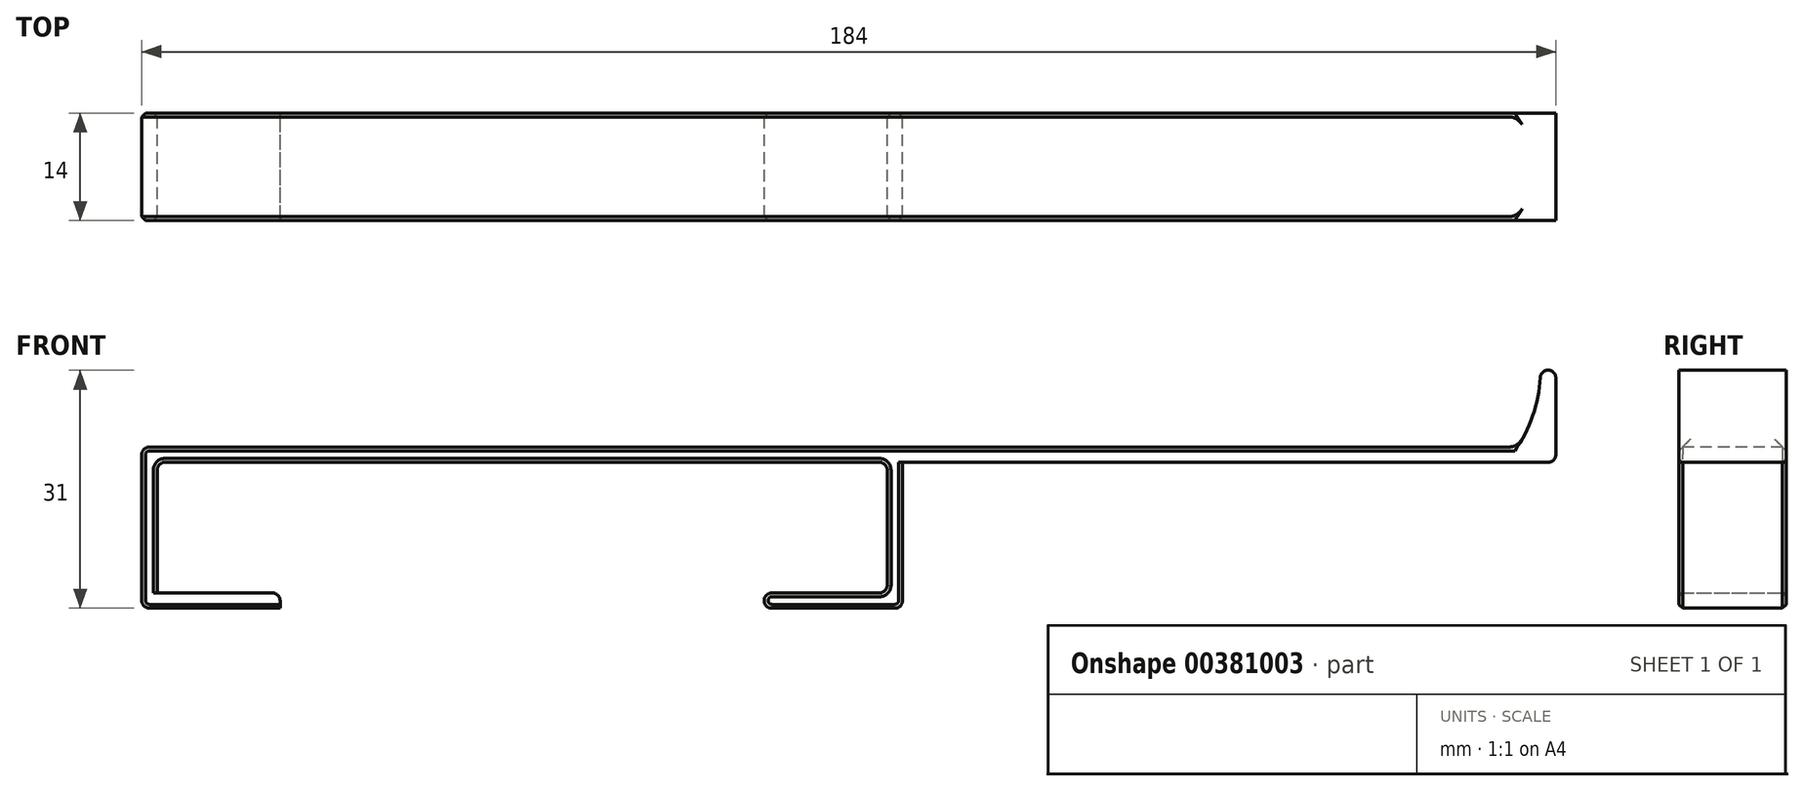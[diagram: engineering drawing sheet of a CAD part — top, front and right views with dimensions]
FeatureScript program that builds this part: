
annotation { "Feature Type Name" : "Feature", "Feature Type Description" : "" }
export const myFeature = defineFeature(function(context is Context, id is Id, definition is map)
    precondition{}
    {
        {
            var Q0;
            Q0=qCreatedBy(makeId("Front.planeOp"),FACE);
            var sketch = newSketch(context, id + "F0", { "sketchPlane" : qUnion([Q0])});
            skLineSegment(sketch, "E0", {"start": v(-167.5, 21) * mm, "end": v(-68.5, 21) * mm});
            skLineSegment(sketch, "E1", {"start": v(-68.5, 19) * mm, "end": v(-68.5, 0) * mm});
            skLineSegment(sketch, "E2", {"start": v(-68.5, 0) * mm, "end": v(-86.5, 0) * mm});
            skLineSegment(sketch, "E3", {"start": v(-86.5, 0) * mm, "end": v(-86.5, 2) * mm});
            skLineSegment(sketch, "E4", {"start": v(-86.5, 2) * mm, "end": v(-70.5, 2) * mm});
            skLineSegment(sketch, "E5", {"start": v(-70.5, 2) * mm, "end": v(-70.5, 19) * mm});
            skLineSegment(sketch, "E6", {"start": v(-70.5, 19) * mm, "end": v(-165.5, 19) * mm});
            skLineSegment(sketch, "E7", {"start": v(-165.5, 19) * mm, "end": v(-165.5, 2) * mm});
            skLineSegment(sketch, "E8", {"start": v(-165.5, 2) * mm, "end": v(-149.5, 2) * mm});
            skLineSegment(sketch, "E9", {"start": v(-149.5, 2) * mm, "end": v(-149.5, 0) * mm});
            skLineSegment(sketch, "E10", {"start": v(-149.5, 0) * mm, "end": v(-167.5, 0) * mm});
            skLineSegment(sketch, "E11", {"start": v(-167.5, 0) * mm, "end": v(-167.5, 21) * mm});
            skLineSegment(sketch, "E12.bottom", {"start": v(-68.5, 19) * mm, "end": v(16.5, 19) * mm});
            skLineSegment(sketch, "E12.top", {"start": v(-63.15, 21) * mm, "end": v(11.5, 21) * mm});
            skPoint(sketch, "E13", {"position": v(16.5, 19) * mm});
            skLineSegment(sketch, "E14", {"start": v(16.5, 21) * mm, "end": v(16.5, 19) * mm});
            skPoint(sketch, "E15.orphan", {"position": v(26.5, 19) * mm});
            skLineSegment(sketch, "E16", {"start": v(16.5, 21) * mm, "end": v(16.5, 31) * mm});
            skLineSegment(sketch, "E17", {"start": v(16.5, 31) * mm, "end": v(14.5, 31) * mm});
            skArc(sketch, "E18", {"start": v(11.5, 21) * mm, "mid": v(13.74, 25.78) * mm, "end": v(14.5, 31) * mm});
            skLineSegment(sketch, "E19", {"start": v(-68.5, 21) * mm, "end": v(-63.15, 21) * mm});
            skPoint(sketch, "E20.end.orphan", {"position": v(14.5, 21) * mm});
            skSolve(sketch);
        }
        {
            var Q0;
            Q0=makeQuery(id+"F0.imprint","IMPRINT",FACE,{"disambiguationData":[TD([[makeQuery(id+"F0.imprint","IMPRINT",EDGE,{"derivedFrom":sQuery(id+"F0.wireOp",EDGE,"E0")}),-1.0]])]});
            extrude(context, id + "F1", {"entities" : qUnion([Q0]), "depth" : 14 * mm});
        }
        {
            var Q0;
            Q0=makeQuery(id+"F1.opExtrude","SWEPT_EDGE",EDGE,{"disambiguationData":[OSD([sQuery(id+"F0.wireOp",EDGE,"E17"),sQuery(id+"F0.wireOp",EDGE,"E18")])]});
            var Q1;
            Q1=makeQuery(id+"F1.opExtrude","SWEPT_EDGE",EDGE,{"disambiguationData":[OSD([sQuery(id+"F0.wireOp",EDGE,"E16"),sQuery(id+"F0.wireOp",EDGE,"E17")])]});
            var Q2;
            Q2=makeQuery(id+"F1.opExtrude","SWEPT_EDGE",EDGE,{"disambiguationData":[OSD([sQuery(id+"F0.wireOp",EDGE,"E12.bottom"),sQuery(id+"F0.wireOp",EDGE,"E14")])]});
            var Q3;
            Q3=makeQuery(id+"F1.opExtrude","SWEPT_EDGE",EDGE,{"disambiguationData":[OSD([sQuery(id+"F0.wireOp",EDGE,"E4"),sQuery(id+"F0.wireOp",EDGE,"E5")])]});
            var Q4;
            Q4=makeQuery(id+"F1.opExtrude","SWEPT_EDGE",EDGE,{"disambiguationData":[OSD([sQuery(id+"F0.wireOp",EDGE,"E5"),sQuery(id+"F0.wireOp",EDGE,"E6")])]});
            var Q5;
            Q5=makeQuery(id+"F1.opExtrude","SWEPT_EDGE",EDGE,{"disambiguationData":[OSD([sQuery(id+"F0.wireOp",EDGE,"E3"),sQuery(id+"F0.wireOp",EDGE,"E4")])]});
            var Q6;
            Q6=makeQuery(id+"F1.opExtrude","SWEPT_EDGE",EDGE,{"disambiguationData":[OSD([sQuery(id+"F0.wireOp",EDGE,"E2"),sQuery(id+"F0.wireOp",EDGE,"E3")])]});
            var Q7;
            Q7=makeQuery(id+"F1.opExtrude","SWEPT_EDGE",EDGE,{"disambiguationData":[OSD([sQuery(id+"F0.wireOp",EDGE,"E1"),sQuery(id+"F0.wireOp",EDGE,"E2")])]});
            var Q8;
            Q8=makeQuery(id+"F1.opExtrude","SWEPT_EDGE",EDGE,{"disambiguationData":[OSD([sQuery(id+"F0.wireOp",EDGE,"E6"),sQuery(id+"F0.wireOp",EDGE,"E7")])]});
            var Q9;
            Q9=makeQuery(id+"F1.opExtrude","SWEPT_EDGE",EDGE,{"disambiguationData":[OSD([sQuery(id+"F0.wireOp",EDGE,"E8"),sQuery(id+"F0.wireOp",EDGE,"E9")])]});
            var Q10;
            Q10=makeQuery(id+"F1.opExtrude","SWEPT_EDGE",EDGE,{"disambiguationData":[OSD([sQuery(id+"F0.wireOp",EDGE,"E10"),sQuery(id+"F0.wireOp",EDGE,"E11")])]});
            var Q11;
            Q11=makeQuery(id+"F1.opExtrude","SWEPT_EDGE",EDGE,{"disambiguationData":[OSD([sQuery(id+"F0.wireOp",EDGE,"E0"),sQuery(id+"F0.wireOp",EDGE,"E11")])]});
            fillet(context, id + "F2", {"entities" : qUnion([Q0, Q1, Q2, Q3, Q4, Q5, Q6, Q7, Q8, Q9, Q10, Q11]), "radius" : 1 * mm, "tangentPropagation" : true, "allowEdgeOverflow" : false});
        }
        {
            var Q0;
            Q0=makeQuery(id+"F1.opExtrude","CAP_EDGE",EDGE,{"disambiguationData":[OSD([sQuery(id+"F0.wireOp",EDGE,"E0"),sQuery(id+"F0.wireOp",EDGE,"E12.top"),sQuery(id+"F0.wireOp",EDGE,"E19")])],"isStart":true});
            var Q1;
            Q1=makeQuery(id+"F1.opExtrude","CAP_EDGE",EDGE,{"disambiguationData":[OSD([sQuery(id+"F0.wireOp",EDGE,"E6")])],"isStart":true});
            var Q2;
            Q2=makeQuery(id+"F1.opExtrude","CAP_EDGE",EDGE,{"disambiguationData":[OSD([sQuery(id+"F0.wireOp",EDGE,"E11")])],"isStart":false});
            var Q3;
            Q3=makeQuery(id+"F1.opExtrude","CAP_EDGE",EDGE,{"disambiguationData":[OSD([sQuery(id+"F0.wireOp",EDGE,"E1")])],"isStart":false});
            chamfer(context, id + "F3", {"entities" : qUnion([Q0, Q1, Q2, Q3]), "width" : .5 * mm, "tangentPropagation" : true});
        }
        {
            var Q0;
            Q0=makeQuery(id+"F1.opExtrude","SWEPT_EDGE",EDGE,{"disambiguationData":[OSD([sQuery(id+"F0.wireOp",EDGE,"E12.top"),sQuery(id+"F0.wireOp",EDGE,"E18")])]});
            fillet(context, id + "F4", {"entities" : qUnion([Q0]), "radius" : 2 * mm, "tangentPropagation" : true, "allowEdgeOverflow" : false});
        }
    });
